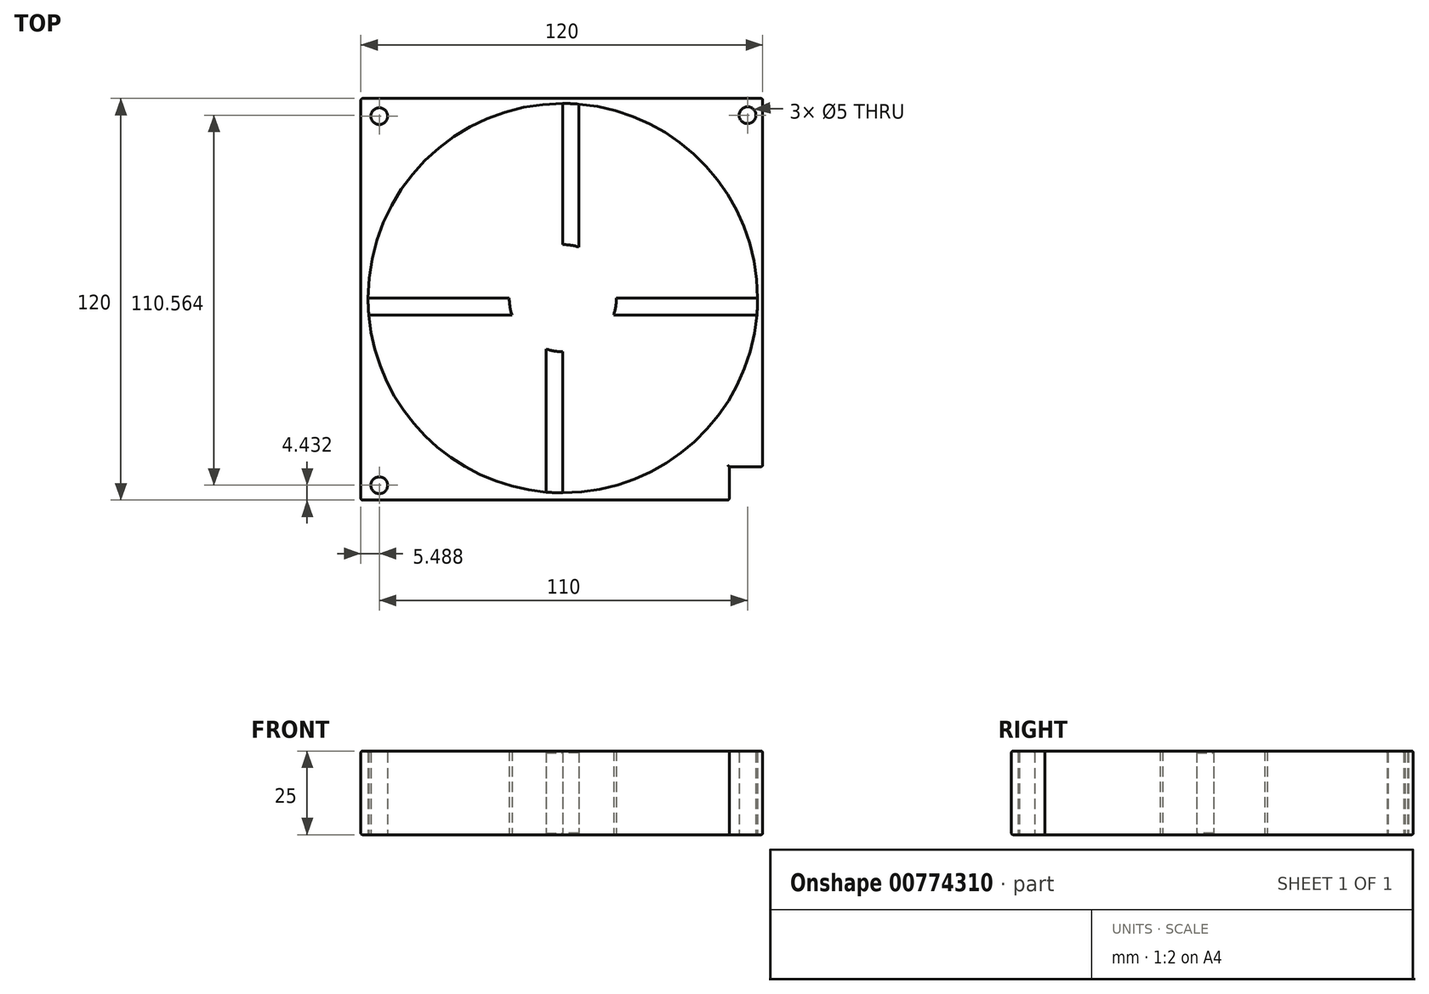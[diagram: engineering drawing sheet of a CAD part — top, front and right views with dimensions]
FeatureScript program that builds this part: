
annotation { "Feature Type Name" : "Feature", "Feature Type Description" : "" }
export const myFeature = defineFeature(function(context is Context, id is Id, definition is map)
    precondition{}
    {
        {
            var Q0;
            Q0=qCreatedBy(makeId("Top.planeOp"),FACE);
            var sketch = newSketch(context, id + "F0", { "sketchPlane" : qUnion([Q0])});
            skLineSegment(sketch, "E0.top", {"start": v(-59, -58.96) * mm, "end": v(61, -58.96) * mm});
            skLineSegment(sketch, "E0.right", {"start": v(61, 61.04) * mm, "end": v(61, -58.96) * mm});
            skLineSegment(sketch, "E1", {"start": v(-49, -48.96) * mm, "end": v(-49, -58.96) * mm});
            skLineSegment(sketch, "E2", {"start": v(61, -58.96) * mm, "end": v(51, -58.96) * mm});
            skLineSegment(sketch, "E3", {"start": v(51, -58.96) * mm, "end": v(51, -48.96) * mm});
            skLineSegment(sketch, "E4", {"start": v(-48.51, 61.04) * mm, "end": v(-48.51, 50.47) * mm});
            skLineSegment(sketch, "E5", {"start": v(-48.51, 50.47) * mm, "end": v(-59, 50.47) * mm});
            skLineSegment(sketch, "E6", {"start": v(51.49, 61.04) * mm, "end": v(51.49, 51.04) * mm});
            skLineSegment(sketch, "E7", {"start": v(51.49, 51.04) * mm, "end": v(61, 51.04) * mm});
            skPoint(sketch, "E8", {"position": v(61, 61.04) * mm});
            skPoint(sketch, "E9", {"position": v(61, 51.04) * mm});
            skCircle(sketch, "E10", {"center": v(-53.51, 55.75) * mm, "radius": 2.5 * mm});
            skLineSegment(sketch, "E11.trimOffspring", {"start": v(-48.51, 61.04) * mm, "end": v(51.49, 61.04) * mm});
            skLineSegment(sketch, "E12", {"start": v(-59, 61.04) * mm, "end": v(-48.51, 61.04) * mm});
            skCircle(sketch, "E13", {"center": v(-53.51, -54.53) * mm, "radius": 2.5 * mm});
            skCircle(sketch, "E14", {"center": v(56.49, -54.53) * mm, "radius": 2.5 * mm});
            skLineSegment(sketch, "E15", {"start": v(-59, -48.96) * mm, "end": v(-49, -48.96) * mm});
            skLineSegment(sketch, "E16", {"start": v(51, -48.96) * mm, "end": v(61, -48.96) * mm});
            skCircle(sketch, "E17", {"center": v(56.49, 56.04) * mm, "radius": 2.5 * mm});
            skLineSegment(sketch, "E18", {"start": v(51.49, 61.04) * mm, "end": v(61, 61.04) * mm});
            skCircle(sketch, "E19", {"center": v(-53.51, -54.53) * mm, "radius": 1.5 * mm});
            skCircle(sketch, "E20", {"center": v(-53.51, 55.75) * mm, "radius": 1.5 * mm});
            skCircle(sketch, "E21", {"center": v(56.49, 56.04) * mm, "radius": 1.5 * mm});
            skCircle(sketch, "E22", {"center": v(56.49, -54.53) * mm, "radius": 1.5 * mm});
            skLineSegment(sketch, "E23", {"start": v(-59, 61.04) * mm, "end": v(-59, -58.96) * mm});
            skCircle(sketch, "E24", {"center": v(1.31, 1.37) * mm, "radius": 58.17 * mm});
            skCircle(sketch, "E25", {"center": v(1.31, 1.37) * mm, "radius": 16 * mm});
            skLineSegment(sketch, "E26", {"start": v(1.31, 17.37) * mm, "end": v(1.31, 59.54) * mm});
            skLineSegment(sketch, "E27", {"start": v(-14.69, 1.37) * mm, "end": v(-56.86, 1.37) * mm});
            skLineSegment(sketch, "E28", {"start": v(1.31, -14.63) * mm, "end": v(1.31, -56.8) * mm});
            skLineSegment(sketch, "E29", {"start": v(17.31, 1.37) * mm, "end": v(59.48, 1.37) * mm});
            skLineSegment(sketch, "E30.0", {"start": v(6.09, 16.64) * mm, "end": v(6.09, 59.34) * mm});
            skLineSegment(sketch, "E31.0", {"start": v(-13.89, -3.63) * mm, "end": v(-56.64, -3.63) * mm});
            skLineSegment(sketch, "E32.0", {"start": v(16.5, -3.63) * mm, "end": v(59.26, -3.63) * mm});
            skLineSegment(sketch, "E33.0", {"start": v(-3.69, -13.83) * mm, "end": v(-3.69, -56.58) * mm});
            skLineSegment(sketch, "E34", {"start": v(-3.69, -13.83) * mm, "end": v(-3.55, -13.87) * mm});
            skSolve(sketch);
        }
        {
            var Q0;
            {var subQ5=sQuery(id+"F0.wireOp",EDGE,"E1");Q0=makeQuery(id+"F0.imprint","IMPRINT",FACE,{"disambiguationData":[TD([[makeQuery(id+"F0.imprint","IMPRINT",EDGE,{"derivedFrom":subQ5}),1.0]])]});}
            var Q1;
            Q1=makeQuery(id+"F0.imprint","IMPRINT",FACE,{"disambiguationData":[TD([[makeQuery(id+"F0.imprint","IMPRINT",EDGE,{"derivedFrom":sQuery(id+"F0.wireOp",EDGE,"E6")}),1.0]])]});
            var Q2;
            Q2=makeQuery(id+"F0.imprint","IMPRINT",FACE,{"disambiguationData":[TD([[makeQuery(id+"F0.imprint","IMPRINT",EDGE,{"derivedFrom":sQuery(id+"F0.wireOp",EDGE,"E4")}),-1.0]])]});
            var Q3;
            {var subQ1=sQuery(id+"F0.wireOp",EDGE,"E1");Q3=makeQuery(id+"F0.imprint","IMPRINT",FACE,{"disambiguationData":[TD([[makeQuery(id+"F0.imprint","IMPRINT",EDGE,{"derivedFrom":subQ1}),-1.0]])]});}
            var Q4;
            {var subQ1=sQuery(id+"F0.wireOp",EDGE,"E2");Q4=makeQuery(id+"F0.imprint","IMPRINT",FACE,{"disambiguationData":[TD([[makeQuery(id+"F0.imprint","IMPRINT",EDGE,{"derivedFrom":subQ1}),-1.0]])]});}
            extrude(context, id + "F1", {"entities" : qUnion([Q0, Q1, Q2, Q3, Q4]), "depth" : 25 * mm, "offsetDistance" : 25 * mm});
        }
        {
            var Q0;
            Q0=makeQuery(id+"F1.opExtrude","CAP_FACE",FACE,{"disambiguationData":[OSD([sQuery(id+"F0.wireOp",EDGE,"E0.top"),sQuery(id+"F0.wireOp",EDGE,"E0.right"),sQuery(id+"F0.wireOp",EDGE,"E2"),sQuery(id+"F0.wireOp",EDGE,"E10"),sQuery(id+"F0.wireOp",EDGE,"E11.trimOffspring"),sQuery(id+"F0.wireOp",EDGE,"E12"),sQuery(id+"F0.wireOp",EDGE,"E13"),sQuery(id+"F0.wireOp",EDGE,"E14"),sQuery(id+"F0.wireOp",EDGE,"E17"),sQuery(id+"F0.wireOp",EDGE,"E18"),sQuery(id+"F0.wireOp",EDGE,"E23"),sQuery(id+"F0.wireOp",EDGE,"E24")])],"isStart":false});
            var Q1;
            Q1=makeQuery(id+"F1.opExtrude","CAP_FACE",FACE,{"disambiguationData":[OSD([sQuery(id+"F0.wireOp",EDGE,"E0.top"),sQuery(id+"F0.wireOp",EDGE,"E0.right"),sQuery(id+"F0.wireOp",EDGE,"E2"),sQuery(id+"F0.wireOp",EDGE,"E10"),sQuery(id+"F0.wireOp",EDGE,"E11.trimOffspring"),sQuery(id+"F0.wireOp",EDGE,"E12"),sQuery(id+"F0.wireOp",EDGE,"E13"),sQuery(id+"F0.wireOp",EDGE,"E14"),sQuery(id+"F0.wireOp",EDGE,"E17"),sQuery(id+"F0.wireOp",EDGE,"E18"),sQuery(id+"F0.wireOp",EDGE,"E23"),sQuery(id+"F0.wireOp",EDGE,"E24")])],"isStart":true});
            var Q2;
            Q2=makeQuery(id+"F1.opExtrude","SWEPT_FACE",FACE,{"disambiguationData":[OSD([sQuery(id+"F0.wireOp",EDGE,"E0.top"),sQuery(id+"F0.wireOp",EDGE,"E2")])]});
            var Q3;
            Q3=makeQuery(id+"F1.opExtrude","SWEPT_FACE",FACE,{"disambiguationData":[OSD([sQuery(id+"F0.wireOp",EDGE,"E0.right")])]});
            var Q4;
            Q4=makeQuery(id+"F1.opExtrude","SWEPT_FACE",FACE,{"disambiguationData":[OSD([sQuery(id+"F0.wireOp",EDGE,"E23")])]});
            var Q5;
            Q5=makeQuery(id+"F1.opExtrude","SWEPT_FACE",FACE,{"disambiguationData":[OSD([sQuery(id+"F0.wireOp",EDGE,"E11.trimOffspring"),sQuery(id+"F0.wireOp",EDGE,"E12"),sQuery(id+"F0.wireOp",EDGE,"E18")])]});
            fillet(context, id + "F2", {"entities" : qUnion([Q0, Q1, Q2, Q3, Q4, Q5]), "radius" : .5 * mm, "tangentPropagation" : true, "allowEdgeOverflow" : false});
        }
        {
            var Q0;
            {var subQ0=sQuery(id+"F0.wireOp",EDGE,"E26");Q0=makeQuery(id+"F0.imprint","IMPRINT",FACE,{"disambiguationData":[TD([[makeQuery(id+"F0.imprint","IMPRINT",EDGE,{"derivedFrom":subQ0}),-1.0]])]});}
            var Q1;
            {var subQ0=sQuery(id+"F0.wireOp",EDGE,"E29");Q1=makeQuery(id+"F0.imprint","IMPRINT",FACE,{"disambiguationData":[TD([[makeQuery(id+"F0.imprint","IMPRINT",EDGE,{"derivedFrom":subQ0}),-1.0]])]});}
            var Q2;
            {var subQ0=sQuery(id+"F0.wireOp",EDGE,"E28");Q2=makeQuery(id+"F0.imprint","IMPRINT",FACE,{"disambiguationData":[TD([[makeQuery(id+"F0.imprint","IMPRINT",EDGE,{"derivedFrom":subQ0}),-1.0]])]});}
            var Q3;
            {var subQ0=sQuery(id+"F0.wireOp",EDGE,"E25");var subQ7=makeQuery(id+"F0.imprint","IMPRINT",VERTEX,{"derivedFrom":subQ0});Q3=makeQuery(id+"F0.imprint","IMPRINT",FACE,{"disambiguationData":[TD([[makeQuery(id+"F0.imprint","IMPRINT",EDGE,{"disambiguationData":[TD([[subQ7,1.0]])],"derivedFrom":subQ0}),1.0]])]});}
            var Q4;
            {var subQ0=sQuery(id+"F0.wireOp",EDGE,"E27");Q4=makeQuery(id+"F0.imprint","IMPRINT",FACE,{"disambiguationData":[TD([[makeQuery(id+"F0.imprint","IMPRINT",EDGE,{"derivedFrom":subQ0}),1.0]])]});}
            extrude(context, id + "F3", {"entities" : qUnion([Q0, Q1, Q2, Q3, Q4]), "operationType" : NewBodyOperationType.ADD, "depth" : 25 * mm, "offsetDistance" : 25 * mm});
        }
    });
